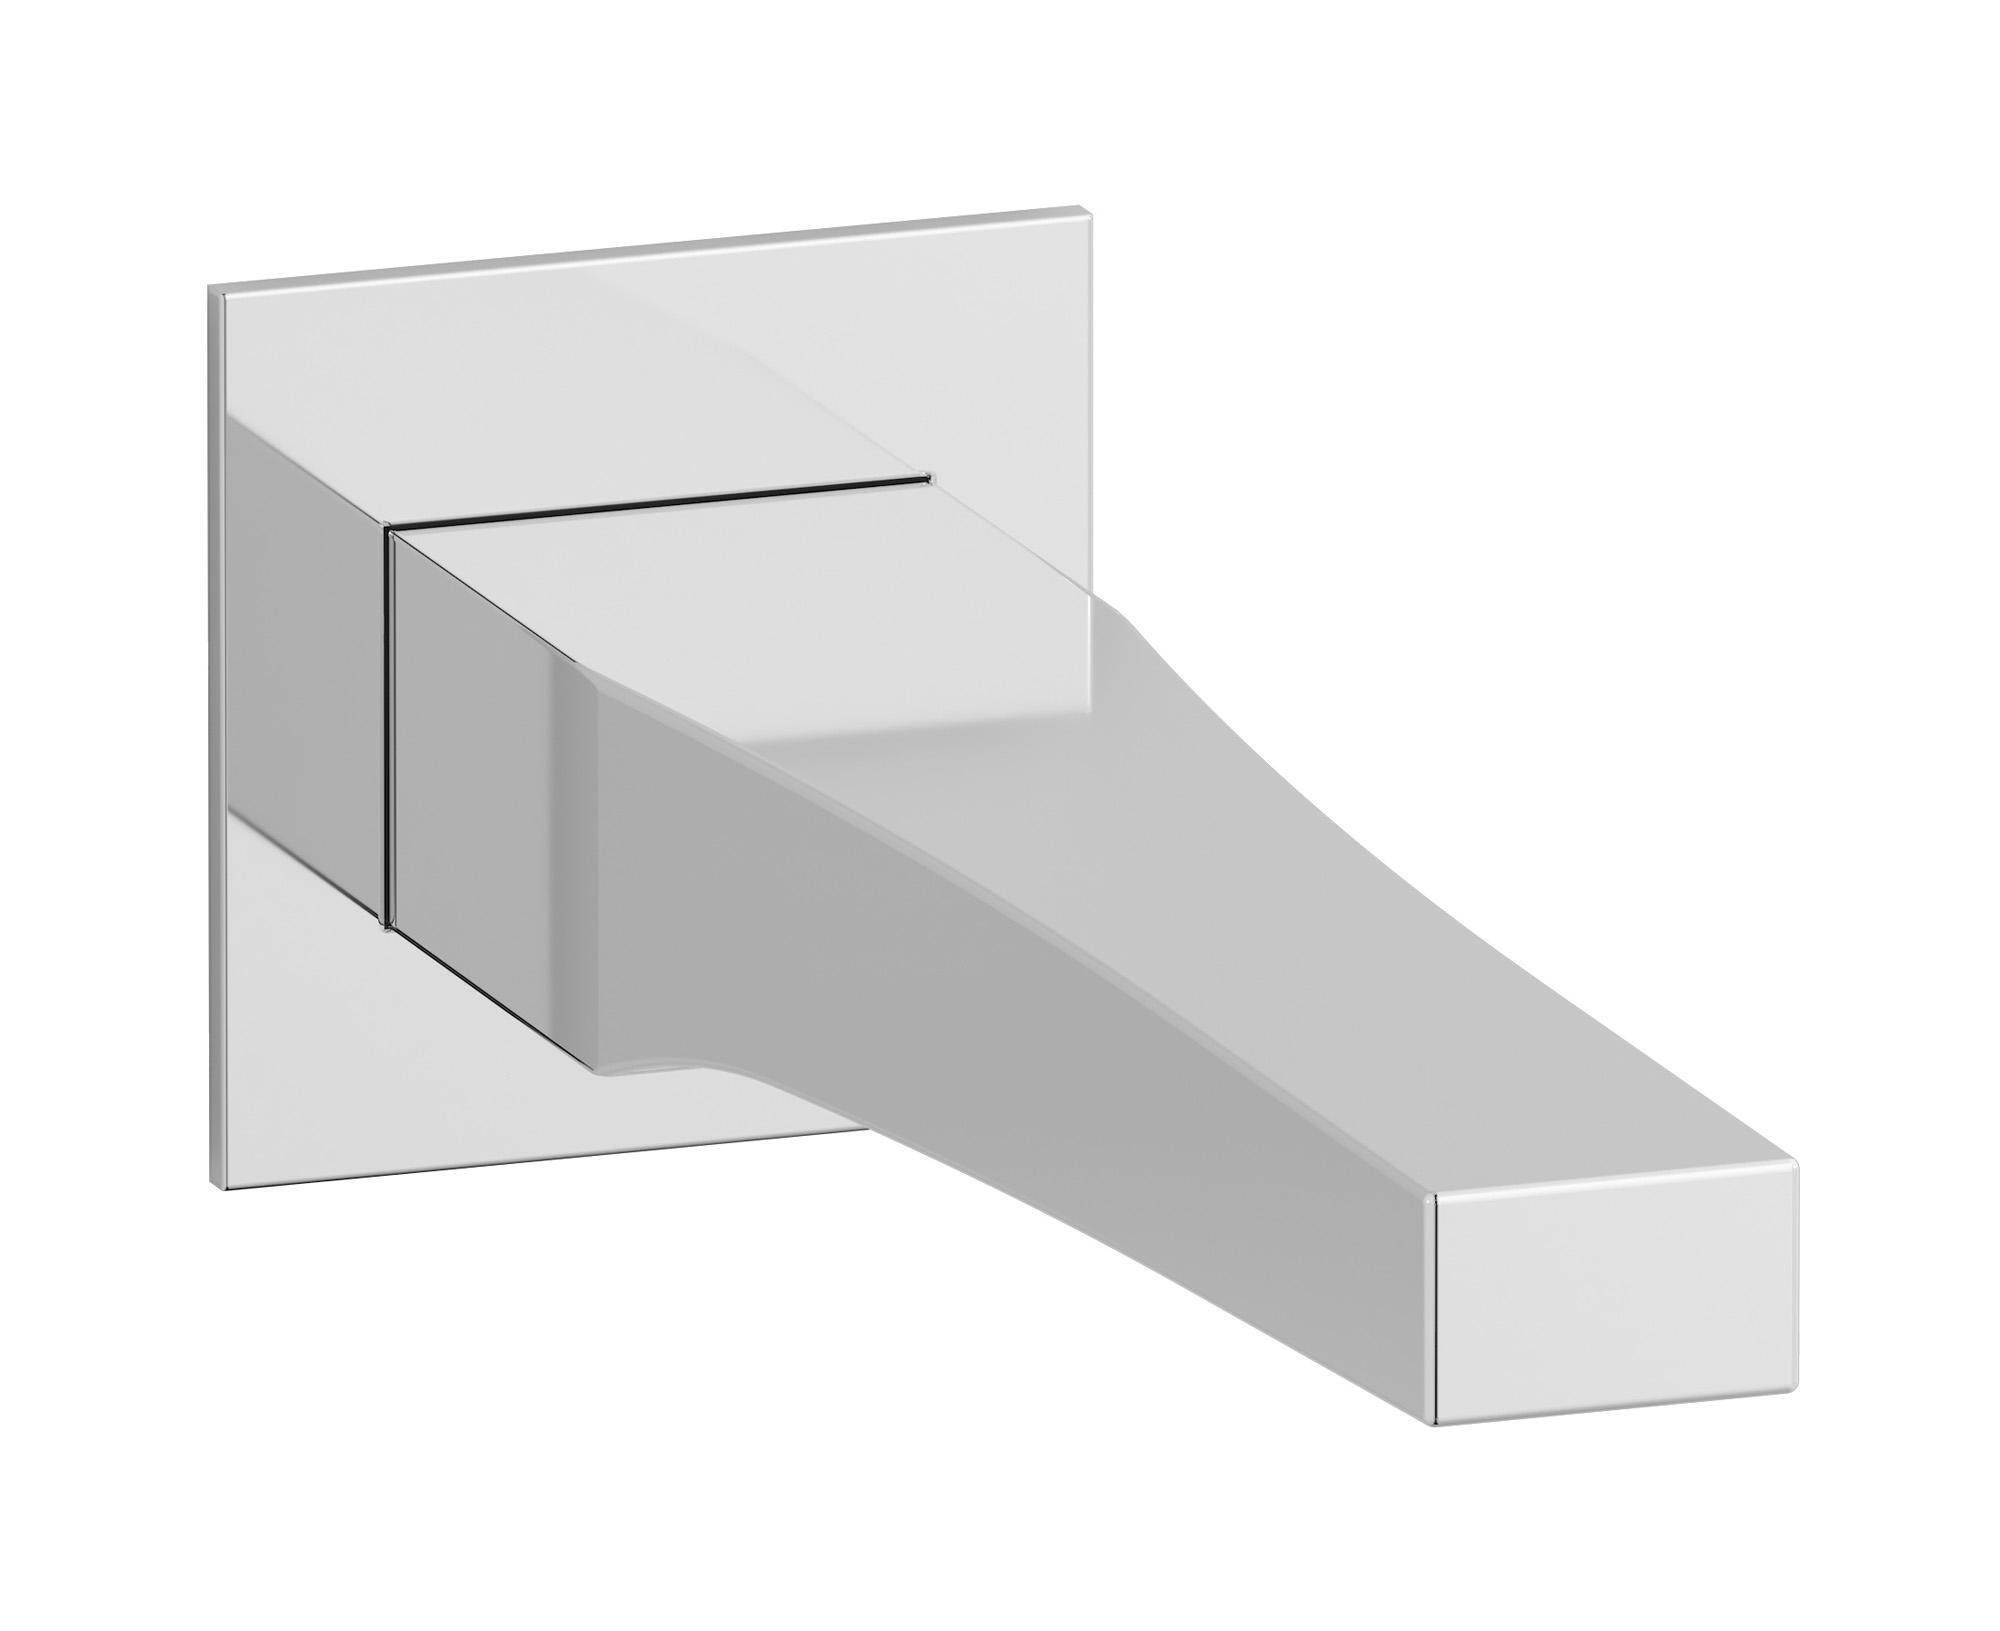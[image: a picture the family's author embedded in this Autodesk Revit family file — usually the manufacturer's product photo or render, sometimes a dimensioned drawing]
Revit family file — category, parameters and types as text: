
# Revit family: TW320
name_source: partatom
category: Apparecchi idraulici
units: mm (PartAtom-declared; Revit-internal decimal feet)

## family parameters
Basato su piano di lavoro = No
Condiviso = No
Mantieni orientamento annotazione = No
Numero OmniClass = 23.45.55.17
Punto di calcolo locali = No
Quota connettore circolare = Usa diametro
Sempre verticale = Sì
Taglio con vuoti quando caricato = No
Tipo di parte = Normale
Titolo OmniClass = Mixing Faucets

## types (12) — shared parameters
Commenti sul tipo = Spout
Connessione CW = No
Connessione HW = No
Connessione di scarico = No
Connessione di ventilazione = No
Descrizione = Wall mounted spout
Produttore = IB Rubinetterie S.p.A.
URL = https://www.weareib.it
Water inlet = 10 mm  [stored 0.0328084 ft]
zero-valued in all types: Prospetto di default

## per-type parameters (varying)
| type | Finishes surface | Immagine tipo | Modello |
| Chrome | IB_Chrome | TW320CC.jpg | TW320CC |
| Brushed nickel | IB_Brushed nickel | TW320SS.jpg | TW320SS |
| Matt black | IB_matt black | TW320NP.jpg | TW320NP |
| Matt white | IB_matt white | TW320BO.jpg | TW320BO |
| Black chrome | IB_Black chrome | TW320CF.jpg | TW320CF |
| Brushed black chrome | IB_Brushed black chrome | TW320CS.jpg | TW320CS |
| Pale gold | IB_Pale gold | TW320II.jpg | TW320II |
| Brushed pale gold | IB_brushed pale gold | TW320IS.jpg | TW320IS |
| Rose gold | IB_Rose gold | TW320RS.jpg | TW320RS |
| Brushed rose gold | IB_Brushed rose gold | TW320SR.jpg | TW320SR |
| Gold | IB_gold | TW320RS.jpg | TW320RS |
| Brushed gold | IB_brushed gold | TW320OS.jpg | TW320OS |

note: [stored X ft] marks values corroborated as IEEE doubles in the binary element streams (Revit-internal decimal feet)
